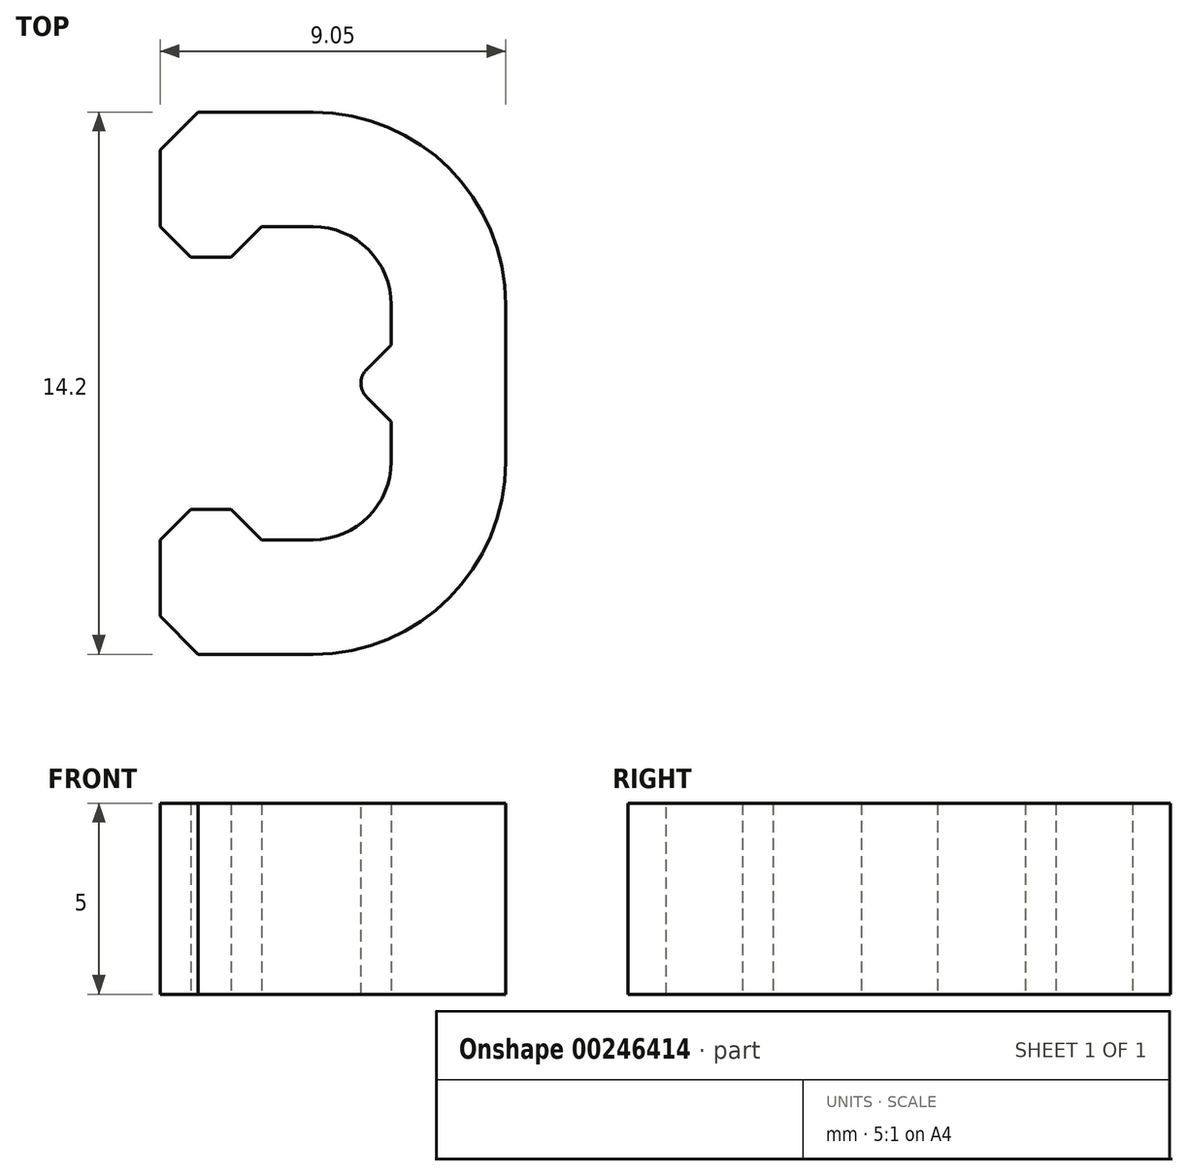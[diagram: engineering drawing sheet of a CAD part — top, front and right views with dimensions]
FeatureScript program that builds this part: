
annotation { "Feature Type Name" : "Feature", "Feature Type Description" : "" }
export const myFeature = defineFeature(function(context is Context, id is Id, definition is map)
    precondition{}
    {
        {
            var Q0;
            Q0=qCreatedBy(makeId("Top.planeOp"),FACE);
            var sketch = newSketch(context, id + "F0", { "sketchPlane" : qUnion([Q0])});
            skArc(sketch, "E0", {"start": v(2.05, 6.15) * mm, "mid": v(1.45, 7.6) * mm, "end": v(0, 8.2) * mm});
            skArc(sketch, "E1", {"start": v(0, 0) * mm, "mid": v(1.45, 0.6) * mm, "end": v(2.05, 2.05) * mm});
            skLineSegment(sketch, "E2", {"start": v(0, 8.2) * mm, "end": v(0, 6.15) * mm});
            skLineSegment(sketch, "E3", {"start": v(0, 0) * mm, "end": v(-4, 0) * mm});
            skLineSegment(sketch, "E4", {"start": v(-4, 0) * mm, "end": v(-4, 8.2) * mm});
            skLineSegment(sketch, "E5", {"start": v(-4, 8.2) * mm, "end": v(0, 8.2) * mm});
            skLineSegment(sketch, "E6", {"start": v(2.05, 6.15) * mm, "end": v(2.05, 2.05) * mm});
            skLineSegment(sketch, "E7.trimOffspring", {"start": v(0, 2.05) * mm, "end": v(0, 0) * mm});
            skCircle(sketch, "E8", {"center": v(0, 2.05) * mm, "radius": 2 * mm});
            skCircle(sketch, "E9", {"center": v(0, 6.15) * mm, "radius": 2 * mm});
            skLineSegment(sketch, "E10.0", {"start": v(0, -3) * mm, "end": v(-4, -3) * mm});
            skLineSegment(sketch, "E10.1", {"start": v(-4, 11.2) * mm, "end": v(0, 11.2) * mm});
            skArc(sketch, "E10.2", {"start": v(5.05, 6.15) * mm, "mid": v(3.57, 9.72) * mm, "end": v(0, 11.2) * mm});
            skLineSegment(sketch, "E10.3", {"start": v(5.05, 6.15) * mm, "end": v(5.05, 2.05) * mm});
            skArc(sketch, "E10.4", {"start": v(0, -3) * mm, "mid": v(3.57, -1.52) * mm, "end": v(5.05, 2.05) * mm});
            skLineSegment(sketch, "E11", {"start": v(-4, 11.2) * mm, "end": v(-4, 8.2) * mm});
            skLineSegment(sketch, "E12", {"start": v(-4, 0) * mm, "end": v(-4, -3) * mm});
            skLineSegment(sketch, "E13", {"start": v(-1.34, 8.2) * mm, "end": v(-2.14, 7.4) * mm});
            skLineSegment(sketch, "E14", {"start": v(-4, 8.2) * mm, "end": v(-3.2, 7.4) * mm});
            skLineSegment(sketch, "E15", {"start": v(-3.2, 7.4) * mm, "end": v(-2.14, 7.4) * mm});
            skLineSegment(sketch, "E16", {"start": v(-4, 0) * mm, "end": v(-3.2, 0.8) * mm});
            skLineSegment(sketch, "E17", {"start": v(-3.2, 0.8) * mm, "end": v(-2.14, 0.8) * mm});
            skLineSegment(sketch, "E18", {"start": v(-2.14, 0.8) * mm, "end": v(-1.34, 0) * mm});
            skLineSegment(sketch, "E19", {"start": v(2.05, 4.1) * mm, "end": v(1.05, 4.1) * mm});
            skLineSegment(sketch, "E20", {"start": v(1.05, 4.1) * mm, "end": v(2.05, 5.1) * mm});
            skLineSegment(sketch, "E21", {"start": v(1.05, 4.1) * mm, "end": v(2.05, 3.1) * mm});
            skSolve(sketch);
        }
        {
            var Q0;
            {var subQ0=sQuery(id+"F0.wireOp",EDGE,"E0");Q0=makeQuery(id+"F0.imprint","IMPRINT",FACE,{"disambiguationData":[TD([[makeQuery(id+"F0.imprint","IMPRINT",EDGE,{"derivedFrom":subQ0}),-1.0]])]});}
            var Q1;
            {var subQ2=sQuery(id+"F0.wireOp",EDGE,"E13");Q1=makeQuery(id+"F0.imprint","IMPRINT",FACE,{"disambiguationData":[TD([[makeQuery(id+"F0.imprint","IMPRINT",EDGE,{"derivedFrom":subQ2}),-1.0]])]});}
            var Q2;
            {var subQ0=sQuery(id+"F0.wireOp",EDGE,"E16");Q2=makeQuery(id+"F0.imprint","IMPRINT",FACE,{"disambiguationData":[TD([[makeQuery(id+"F0.imprint","IMPRINT",EDGE,{"derivedFrom":subQ0}),-1.0]])]});}
            var Q3;
            {var subQ0=sQuery(id+"F0.wireOp",EDGE,"E19");Q3=makeQuery(id+"F0.imprint","IMPRINT",FACE,{"disambiguationData":[TD([[makeQuery(id+"F0.imprint","IMPRINT",EDGE,{"derivedFrom":subQ0}),-1.0]])]});}
            var Q4;
            {var subQ0=sQuery(id+"F0.wireOp",EDGE,"E19");Q4=makeQuery(id+"F0.imprint","IMPRINT",FACE,{"disambiguationData":[TD([[makeQuery(id+"F0.imprint","IMPRINT",EDGE,{"derivedFrom":subQ0}),1.0]])]});}
            extrude(context, id + "F1", {"entities" : qUnion([Q0, Q1, Q2, Q3, Q4]), "depth" : 5 * mm});
        }
        {
            var Q0;
            Q0=makeQuery(id+"F1.opExtrude","SWEPT_EDGE",EDGE,{"disambiguationData":[OSD([sQuery(id+"F0.wireOp",EDGE,"E10.1"),sQuery(id+"F0.wireOp",EDGE,"E11")])]});
            var Q1;
            Q1=makeQuery(id+"F1.opExtrude","SWEPT_EDGE",EDGE,{"disambiguationData":[OSD([sQuery(id+"F0.wireOp",EDGE,"E10.0"),sQuery(id+"F0.wireOp",EDGE,"E12")])]});
            chamfer(context, id + "F2", {"entities" : qUnion([Q0, Q1]), "width" : 1 * mm, "tangentPropagation" : true});
        }
        {
            var Q0;
            Q0=makeQuery(id+"F1.opExtrude","SWEPT_EDGE",EDGE,{"disambiguationData":[OSD([sQuery(id+"F0.wireOp",EDGE,"E19"),sQuery(id+"F0.wireOp",EDGE,"E20"),sQuery(id+"F0.wireOp",EDGE,"E21")])]});
            fillet(context, id + "F3", {"entities" : qUnion([Q0]), "radius" : 0.5 * mm, "tangentPropagation" : true, "allowEdgeOverflow" : false});
        }
    });
